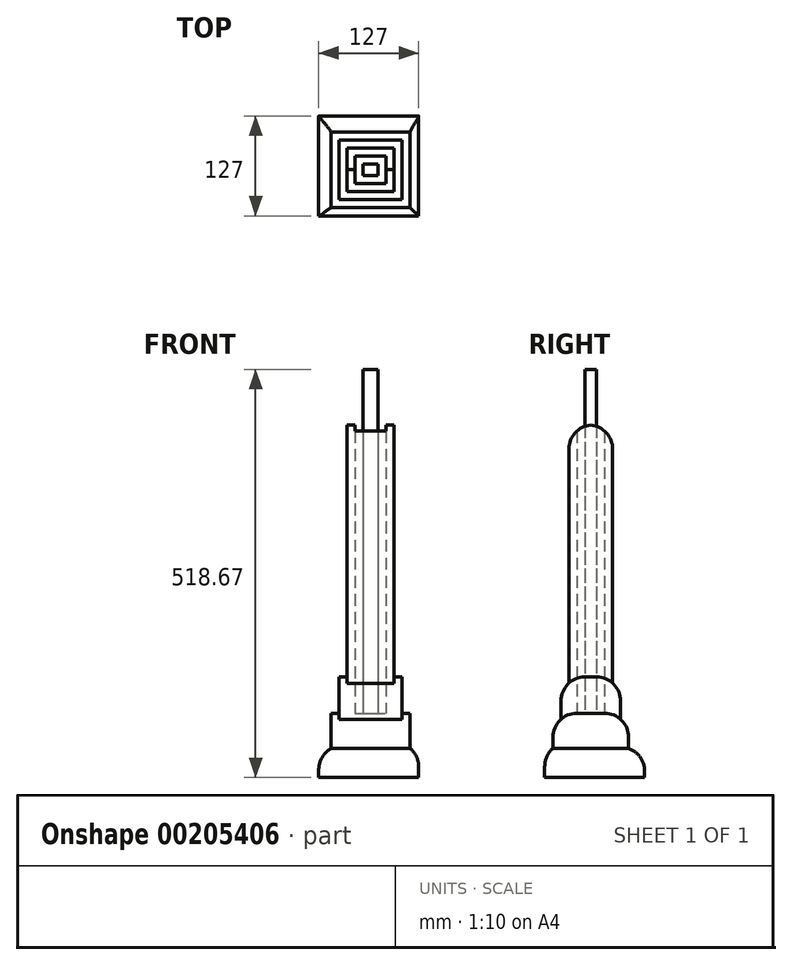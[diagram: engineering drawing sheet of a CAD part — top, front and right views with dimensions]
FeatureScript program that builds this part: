
annotation { "Feature Type Name" : "Feature", "Feature Type Description" : "" }
export const myFeature = defineFeature(function(context is Context, id is Id, definition is map)
    precondition{}
    {
        {
            var Q0;
            Q0=qCreatedBy(makeId("Top.planeOp"),FACE);
            var sketch = newSketch(context, id + "F0", { "sketchPlane" : qUnion([Q0])});
            skLineSegment(sketch, "E0.bottom", {"start": v(-76.64, 60.51) * mm, "end": v(50.36, 60.51) * mm});
            skLineSegment(sketch, "E0.top", {"start": v(-76.64, -66.49) * mm, "end": v(50.36, -66.49) * mm});
            skLineSegment(sketch, "E0.left", {"start": v(-76.64, 60.51) * mm, "end": v(-76.64, -66.49) * mm});
            skLineSegment(sketch, "E0.right", {"start": v(50.36, 60.51) * mm, "end": v(50.36, -66.49) * mm});
            skLineSegment(sketch, "E1.bottom", {"start": v(-60.88, 40.16) * mm, "end": v(39.38, 40.16) * mm});
            skLineSegment(sketch, "E1.top", {"start": v(-60.88, -56.11) * mm, "end": v(39.38, -56.11) * mm});
            skLineSegment(sketch, "E1.left", {"start": v(-60.88, 40.16) * mm, "end": v(-60.88, -56.11) * mm});
            skLineSegment(sketch, "E1.right", {"start": v(39.38, 40.16) * mm, "end": v(39.38, -56.11) * mm});
            skSolve(sketch);
        }
        {
            var Q0;
            Q0=makeQuery(id+"F0.imprint","IMPRINT",FACE,{"disambiguationData":[TD([[makeQuery(id+"F0.imprint","IMPRINT",EDGE,{"derivedFrom":sQuery(id+"F0.wireOp",EDGE,"E1.bottom")}),-1.0]])]});
            extrude(context, id + "F1", {"entities" : qUnion([Q0]), "depth" : 81.8 * mm});
        }
        {
            var Q0;
            Q0=makeQuery(id+"F0.imprint","IMPRINT",FACE,{"disambiguationData":[TD([[makeQuery(id+"F0.imprint","IMPRINT",EDGE,{"derivedFrom":sQuery(id+"F0.wireOp",EDGE,"E0.bottom")}),-1.0]])]});
            extrude(context, id + "F2", {"entities" : qUnion([Q0]), "operationType" : NewBodyOperationType.ADD, "depth" : 3.8 * mm});
        }
        {
            var Q0;
            Q0=makeQuery(id+"F2.opExtrude","CAP_FACE",FACE,{"disambiguationData":[OSD([sQuery(id+"F0.wireOp",EDGE,"E0.bottom"),sQuery(id+"F0.wireOp",EDGE,"E0.top"),sQuery(id+"F0.wireOp",EDGE,"E0.left"),sQuery(id+"F0.wireOp",EDGE,"E0.right"),sQuery(id+"F0.wireOp",EDGE,"E1.bottom"),sQuery(id+"F0.wireOp",EDGE,"E1.top"),sQuery(id+"F0.wireOp",EDGE,"E1.left"),sQuery(id+"F0.wireOp",EDGE,"E1.right")])],"isStart":false});
            extrude(context, id + "F3", {"entities" : qUnion([Q0]), "operationType" : NewBodyOperationType.ADD, "depth" : 33.27 * mm});
        }
        {
            var Q0;
            Q0=makeQuery(id+"F1.opExtrude","CAP_FACE",FACE,{"disambiguationData":[OSD([sQuery(id+"F0.wireOp",EDGE,"E1.bottom"),sQuery(id+"F0.wireOp",EDGE,"E1.top"),sQuery(id+"F0.wireOp",EDGE,"E1.left"),sQuery(id+"F0.wireOp",EDGE,"E1.right")])],"isStart":false});
            var sketch = newSketch(context, id + "F4", { "sketchPlane" : qUnion([Q0])});
            skLineSegment(sketch, "E2.bottom", {"start": v(-50.72, 30) * mm, "end": v(29.22, 30) * mm});
            skLineSegment(sketch, "E2.top", {"start": v(-50.72, -45.95) * mm, "end": v(29.22, -45.95) * mm});
            skLineSegment(sketch, "E2.left", {"start": v(-50.72, 30) * mm, "end": v(-50.72, -45.95) * mm});
            skLineSegment(sketch, "E2.right", {"start": v(29.22, 30) * mm, "end": v(29.22, -45.95) * mm});
            skLineSegment(sketch, "E3.bottom", {"start": v(-40.56, 19.84) * mm, "end": v(19.06, 19.84) * mm});
            skLineSegment(sketch, "E3.top", {"start": v(-40.56, -35.8) * mm, "end": v(19.06, -35.8) * mm});
            skLineSegment(sketch, "E3.left", {"start": v(-40.56, 19.84) * mm, "end": v(-40.56, -35.8) * mm});
            skLineSegment(sketch, "E3.right", {"start": v(19.06, 19.84) * mm, "end": v(19.06, -35.8) * mm});
            skLineSegment(sketch, "E4.bottom", {"start": v(-30.4, 9.68) * mm, "end": v(8.9, 9.68) * mm});
            skLineSegment(sketch, "E4.top", {"start": v(-30.4, -25.63) * mm, "end": v(8.9, -25.63) * mm});
            skLineSegment(sketch, "E4.left", {"start": v(-30.4, 9.68) * mm, "end": v(-30.4, -25.63) * mm});
            skLineSegment(sketch, "E4.right", {"start": v(8.9, 9.68) * mm, "end": v(8.9, -25.63) * mm});
            skLineSegment(sketch, "E5.bottom", {"start": v(-20.24, -0.48) * mm, "end": v(-1.26, -0.48) * mm});
            skLineSegment(sketch, "E5.top", {"start": v(-20.24, -15.47) * mm, "end": v(-1.26, -15.47) * mm});
            skLineSegment(sketch, "E5.left", {"start": v(-20.24, -0.48) * mm, "end": v(-20.24, -15.47) * mm});
            skLineSegment(sketch, "E5.right", {"start": v(-1.26, -0.48) * mm, "end": v(-1.26, -15.47) * mm});
            skSolve(sketch);
        }
        {
            var Q0;
            Q0=makeQuery(id+"F4.imprint","IMPRINT",FACE,{"disambiguationData":[TD([[makeQuery(id+"F4.imprint","IMPRINT",EDGE,{"derivedFrom":sQuery(id+"F4.wireOp",EDGE,"E2.bottom")}),-1.0]])]});
            extrude(context, id + "F5", {"entities" : qUnion([Q0]), "operationType" : NewBodyOperationType.ADD, "depth" : 45.97 * mm});
        }
        {
            var Q0;
            Q0=makeQuery(id+"F4.imprint","IMPRINT",FACE,{"disambiguationData":[TD([[makeQuery(id+"F4.imprint","IMPRINT",EDGE,{"derivedFrom":sQuery(id+"F4.wireOp",EDGE,"E3.bottom")}),-1.0]])]});
            extrude(context, id + "F6", {"entities" : qUnion([Q0]), "operationType" : NewBodyOperationType.ADD, "depth" : 366.27 * mm});
        }
        {
            var Q0;
            Q0=makeQuery(id+"F4.imprint","IMPRINT",FACE,{"disambiguationData":[TD([[makeQuery(id+"F4.imprint","IMPRINT",EDGE,{"derivedFrom":sQuery(id+"F4.wireOp",EDGE,"E5.bottom")}),-1.0]])]});
            extrude(context, id + "F7", {"entities" : qUnion([Q0]), "operationType" : NewBodyOperationType.ADD, "depth" : 436.88 * mm});
        }
        {
            var Q0;
            Q0=makeQuery(id+"F3.opExtrude","CAP_EDGE",EDGE,{"disambiguationData":[OSD([sQuery(id+"F0.wireOp",EDGE,"E0.right")])],"isStart":false});
            var Q1;
            Q1=makeQuery(id+"F3.opExtrude","CAP_EDGE",EDGE,{"disambiguationData":[OSD([sQuery(id+"F0.wireOp",EDGE,"E0.bottom")])],"isStart":false});
            var Q2;
            Q2=makeQuery(id+"F3.opExtrude","CAP_EDGE",EDGE,{"disambiguationData":[OSD([sQuery(id+"F0.wireOp",EDGE,"E0.top")])],"isStart":false});
            var Q3;
            Q3=makeQuery(id+"F3.opExtrude","CAP_EDGE",EDGE,{"disambiguationData":[OSD([sQuery(id+"F0.wireOp",EDGE,"E0.left")])],"isStart":false});
            var Q4;
            Q4=makeQuery(id+"F1.opExtrude","CAP_EDGE",EDGE,{"disambiguationData":[OSD([sQuery(id+"F0.wireOp",EDGE,"E1.top")])],"isStart":false});
            var Q5;
            Q5=makeQuery(id+"F5.opExtrude","CAP_EDGE",EDGE,{"disambiguationData":[OSD([sQuery(id+"F4.wireOp",EDGE,"E2.top")])],"isStart":false});
            var Q6;
            Q6=makeQuery(id+"F6.opExtrude","CAP_EDGE",EDGE,{"disambiguationData":[OSD([sQuery(id+"F4.wireOp",EDGE,"E3.top")])],"isStart":false});
            var Q7;
            Q7=makeQuery(id+"F1.opExtrude","CAP_EDGE",EDGE,{"disambiguationData":[OSD([sQuery(id+"F0.wireOp",EDGE,"E1.bottom")])],"isStart":false});
            var Q8;
            Q8=makeQuery(id+"F5.opExtrude","CAP_EDGE",EDGE,{"disambiguationData":[OSD([sQuery(id+"F4.wireOp",EDGE,"E2.bottom")])],"isStart":false});
            var Q9;
            Q9=makeQuery(id+"F6.opExtrude","CAP_EDGE",EDGE,{"disambiguationData":[OSD([sQuery(id+"F4.wireOp",EDGE,"E3.bottom")])],"isStart":false});
            fillet(context, id + "F8", {"entities" : qUnion([Q0, Q1, Q2, Q3, Q4, Q5, Q6, Q7, Q8, Q9]), "radius" : 30.66 * mm, "tangentPropagation" : true, "allowEdgeOverflow" : false});
        }
    });
